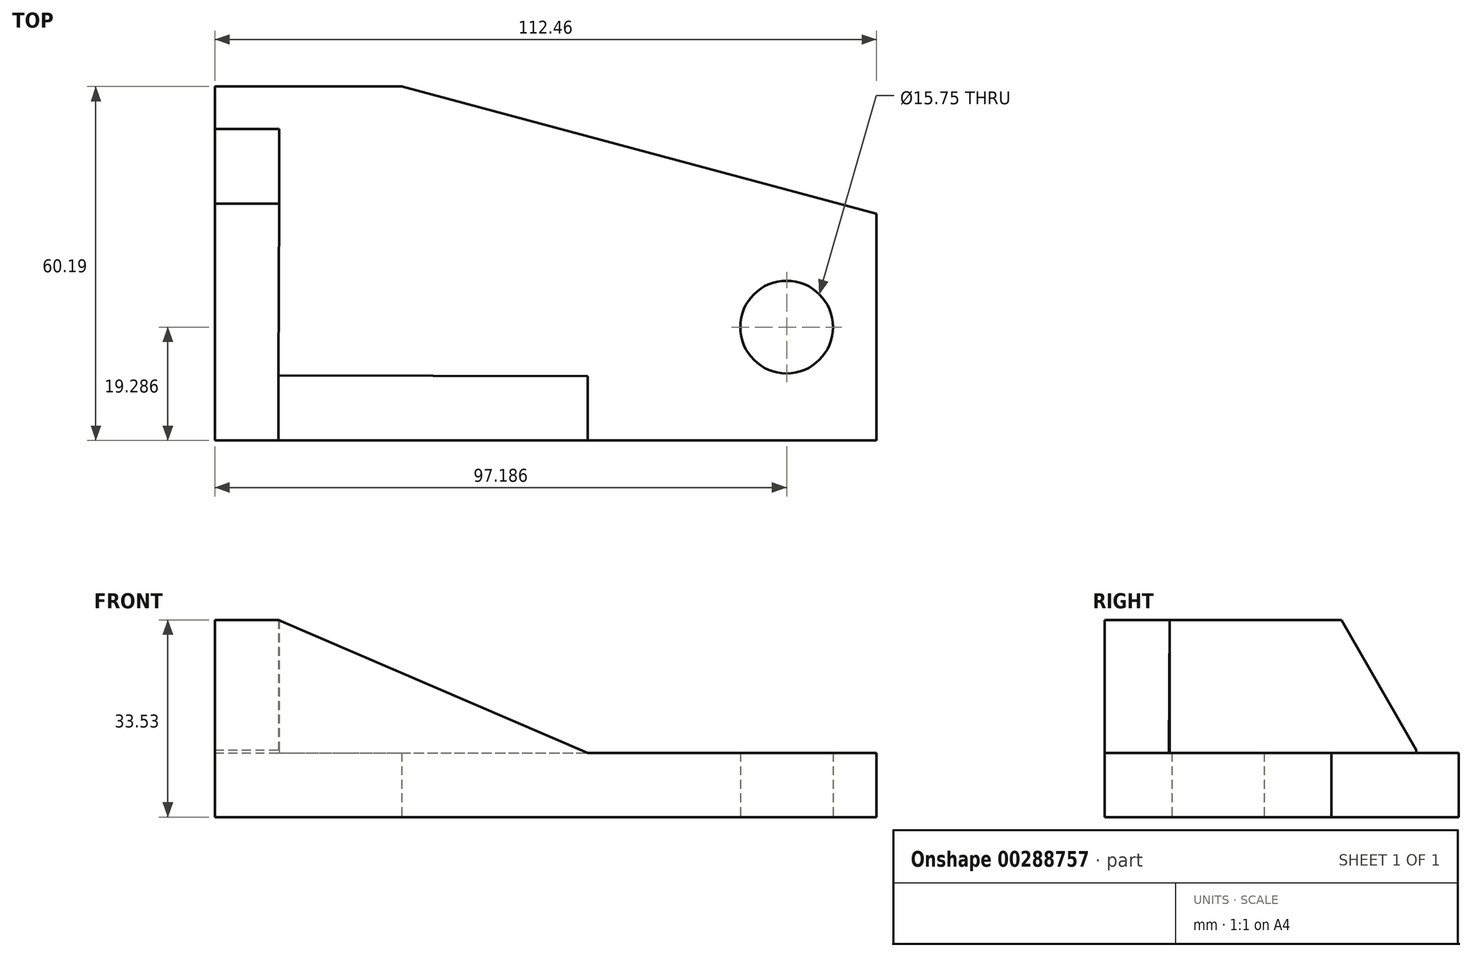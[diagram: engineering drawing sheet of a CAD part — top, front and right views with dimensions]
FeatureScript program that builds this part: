
annotation { "Feature Type Name" : "Feature", "Feature Type Description" : "" }
export const myFeature = defineFeature(function(context is Context, id is Id, definition is map)
    precondition{}
    {
        {
            var Q0;
            Q0=qCreatedBy(makeId("Top.planeOp"),FACE);
            var sketch = newSketch(context, id + "F0", { "sketchPlane" : qUnion([Q0])});
            skLineSegment(sketch, "E0.bottom", {"start": v(-47.23, 28.78) * mm, "end": v(-15.45, 28.78) * mm});
            skLineSegment(sketch, "E0.top", {"start": v(-47.23, -31.41) * mm, "end": v(-15.45, -31.41) * mm});
            skLineSegment(sketch, "E0.left", {"start": v(-47.23, 28.78) * mm, "end": v(-47.23, -31.41) * mm});
            skLineSegment(sketch, "E1", {"start": v(-47.23, 21.6) * mm, "end": v(-36.3, 21.6) * mm});
            skLineSegment(sketch, "E2", {"start": v(-15.45, 28.78) * mm, "end": v(65.23, 7.17) * mm});
            skLineSegment(sketch, "E3", {"start": v(65.23, 7.17) * mm, "end": v(65.23, -31.41) * mm});
            skLineSegment(sketch, "E4", {"start": v(65.23, -31.41) * mm, "end": v(-15.45, -31.41) * mm});
            skCircle(sketch, "E5", {"center": v(49.96, -12.12) * mm, "radius": 7.87 * mm});
            skPoint(sketch, "E5.centerSnap0", {"position": v(49.96, -13.94) * mm});
            skPoint(sketch, "E6.start.orphan", {"position": v(65.23, -12.12) * mm});
            skLineSegment(sketch, "E7.trimOffspring", {"start": v(49.96, -12.12) * mm, "end": v(49.96, 3.54) * mm});
            skPoint(sketch, "E8.orphan", {"position": v(49.96, -31.41) * mm});
            skLineSegment(sketch, "E9", {"start": v(-36.45, -31.41) * mm, "end": v(-36.3, 21.6) * mm});
            skPoint(sketch, "E10.end.orphan", {"position": v(16.3, -31.41) * mm});
            skLineSegment(sketch, "E11", {"start": v(-36.42, -20.35) * mm, "end": v(16.16, -20.5) * mm});
            skLineSegment(sketch, "E12", {"start": v(16.16, -20.5) * mm, "end": v(16.3, -31.41) * mm});
            skSolve(sketch);
        }
        {
            var Q0;
            {var subQ1=sQuery(id+"F0.wireOp",EDGE,"E0.bottom");Q0=makeQuery(id+"F0.imprint","IMPRINT",FACE,{"disambiguationData":[TD([[makeQuery(id+"F0.imprint","IMPRINT",EDGE,{"derivedFrom":subQ1}),-1.0]])]});}
            extrude(context, id + "F1", {"entities" : qUnion([Q0]), "depth" : 10.92 * mm});
        }
        {
            var Q0;
            {var subQ0=sQuery(id+"F0.wireOp",EDGE,"E1");Q0=makeQuery(id+"F0.imprint","IMPRINT",FACE,{"disambiguationData":[TD([[makeQuery(id+"F0.imprint","IMPRINT",EDGE,{"derivedFrom":subQ0}),-1.0]])]});}
            var Q1;
            {var subQ0=sQuery(id+"F0.wireOp",EDGE,"E11");Q1=makeQuery(id+"F0.imprint","IMPRINT",FACE,{"disambiguationData":[TD([[makeQuery(id+"F0.imprint","IMPRINT",EDGE,{"derivedFrom":subQ0}),-1.0]])]});}
            extrude(context, id + "F2", {"entities" : qUnion([Q0, Q1]), "operationType" : NewBodyOperationType.ADD, "depth" : 33.53 * mm});
        }
        {
            var Q0;
            Q0=makeQuery(id+"F2.opExtrude","SWEPT_FACE",FACE,{"disambiguationData":[OSD([sQuery(id+"F0.wireOp",EDGE,"E11")])]});
            var sketch = newSketch(context, id + "F3", { "sketchPlane" : qUnion([Q0])});
            skLineSegment(sketch, "E13", {"start": v(36.37, 33.53) * mm, "end": v(-16.21, 10.92) * mm});
            skSolve(sketch);
        }
        {
            var Q0;
            Q0=makeQuery(id+"F3.imprint","IMPRINT",FACE,{"disambiguationData":[TD([[makeQuery(id+"F3.imprint","IMPRINT",EDGE,{"derivedFrom":sQuery(id+"F3.wireOp",EDGE,"E13")}),-1.0]])]});
            var Q1;
            Q1=makeQuery(id+"F2.opExtrude","SWEPT_FACE",FACE,{"disambiguationData":[OSD([sQuery(id+"F0.wireOp",EDGE,"E12")])]});
            extrude(context, id + "F4", {"entities" : qUnion([Q0, Q1]), "operationType" : NewBodyOperationType.REMOVE, "oppositeDirection" : true, "depth" : 53.6 * mm});
        }
        {
            var Q0;
            Q0=makeQuery(id+"F2.opExtrude","CAP_EDGE",EDGE,{"disambiguationData":[OSD([sQuery(id+"F0.wireOp",EDGE,"E1")])],"isStart":false});
            chamfer(context, id + "F5", {"entities" : qUnion([Q0]), "chamferType" : ChamferType.OFFSET_ANGLE, "width" : 22.1 * mm, "oppositeDirection" : false, "angle" : 30 * degree, "tangentPropagation" : true});
        }
    });
